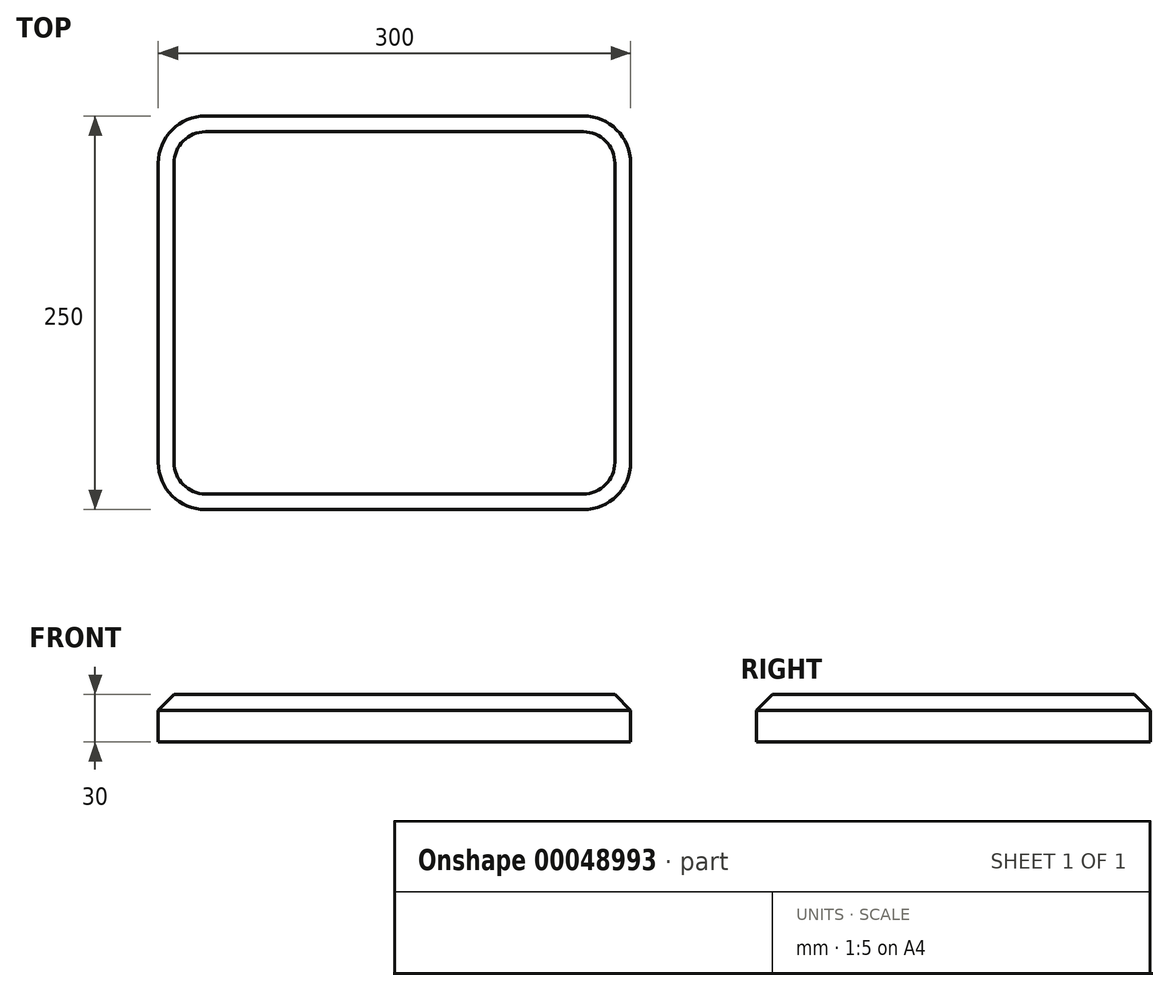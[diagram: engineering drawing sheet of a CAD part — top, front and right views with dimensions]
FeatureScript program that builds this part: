
annotation { "Feature Type Name" : "Feature", "Feature Type Description" : "" }
export const myFeature = defineFeature(function(context is Context, id is Id, definition is map)
    precondition{}
    {
        {
            var Q0;
            Q0=qCreatedBy(makeId("Top.planeOp"),FACE);
            var sketch = newSketch(context, id + "F0", { "sketchPlane" : qUnion([Q0])});
            skLineSegment(sketch, "E0.rect.bottom", {"start": v(150, 125) * mm, "end": v(-150, 125) * mm});
            skLineSegment(sketch, "E0.rect.top", {"start": v(150, -125) * mm, "end": v(-150, -125) * mm});
            skLineSegment(sketch, "E0.rect.left", {"start": v(150, 125) * mm, "end": v(150, -125) * mm});
            skLineSegment(sketch, "E0.rect.right", {"start": v(-150, 125) * mm, "end": v(-150, -125) * mm});
            skPoint(sketch, "E0.rect.middle", {"position": v(0, 0) * mm});
            skSolve(sketch);
        }
        {
            var Q0;
            Q0=makeQuery(id+"F0.imprint","IMPRINT",FACE,{"disambiguationData":[TD([[makeQuery(id+"F0.imprint","IMPRINT",EDGE,{"derivedFrom":sQuery(id+"F0.wireOp",EDGE,"E0.rect.bottom")}),1.0]])]});
            extrude(context, id + "F1", {"entities" : qUnion([Q0]), "depth" : 30 * mm});
        }
        {
            var Q0;
            Q0=makeQuery(id+"F3.opChamfer","BLEND_EDGE",EDGE,{"blendedFrom":[makeQuery(id+"F1.opExtrude","CAP_EDGE",EDGE,{"disambiguationData":[OSD([sQuery(id+"F0.wireOp",EDGE,"E0.rect.top")])],"isStart":false}),makeQuery(id+"F1.opExtrude","CAP_EDGE",EDGE,{"disambiguationData":[OSD([sQuery(id+"F0.wireOp",EDGE,"E0.rect.right")])],"isStart":false})],"blendedInto":[]});
            var Q1;
            Q1=makeQuery(id+"F3.opChamfer","BLEND_EDGE",EDGE,{"blendedFrom":[makeQuery(id+"F1.opExtrude","CAP_EDGE",EDGE,{"disambiguationData":[OSD([sQuery(id+"F0.wireOp",EDGE,"E0.rect.bottom")])],"isStart":false}),makeQuery(id+"F1.opExtrude","CAP_EDGE",EDGE,{"disambiguationData":[OSD([sQuery(id+"F0.wireOp",EDGE,"E0.rect.right")])],"isStart":false})],"blendedInto":[]});
            var Q2;
            Q2=makeQuery(id+"F3.opChamfer","BLEND_EDGE",EDGE,{"blendedFrom":[makeQuery(id+"F1.opExtrude","CAP_EDGE",EDGE,{"disambiguationData":[OSD([sQuery(id+"F0.wireOp",EDGE,"E0.rect.top")])],"isStart":false}),makeQuery(id+"F1.opExtrude","CAP_EDGE",EDGE,{"disambiguationData":[OSD([sQuery(id+"F0.wireOp",EDGE,"E0.rect.left")])],"isStart":false})],"blendedInto":[]});
            var Q3;
            Q3=makeQuery(id+"F3.opChamfer","BLEND_EDGE",EDGE,{"blendedFrom":[makeQuery(id+"F1.opExtrude","CAP_EDGE",EDGE,{"disambiguationData":[OSD([sQuery(id+"F0.wireOp",EDGE,"E0.rect.bottom")])],"isStart":false}),makeQuery(id+"F1.opExtrude","CAP_EDGE",EDGE,{"disambiguationData":[OSD([sQuery(id+"F0.wireOp",EDGE,"E0.rect.left")])],"isStart":false})],"blendedInto":[]});
            var Q4;
            Q4=makeQuery(id+"F1.opExtrude","SWEPT_EDGE",EDGE,{"disambiguationData":[OSD([sQuery(id+"F0.wireOp",EDGE,"E0.rect.top"),sQuery(id+"F0.wireOp",EDGE,"E0.rect.right")])]});
            var Q5;
            Q5=makeQuery(id+"F1.opExtrude","SWEPT_EDGE",EDGE,{"disambiguationData":[OSD([sQuery(id+"F0.wireOp",EDGE,"E0.rect.bottom"),sQuery(id+"F0.wireOp",EDGE,"E0.rect.right")])]});
            var Q6;
            Q6=makeQuery(id+"F1.opExtrude","SWEPT_EDGE",EDGE,{"disambiguationData":[OSD([sQuery(id+"F0.wireOp",EDGE,"E0.rect.bottom"),sQuery(id+"F0.wireOp",EDGE,"E0.rect.left")])]});
            var Q7;
            Q7=makeQuery(id+"F1.opExtrude","SWEPT_EDGE",EDGE,{"disambiguationData":[OSD([sQuery(id+"F0.wireOp",EDGE,"E0.rect.top"),sQuery(id+"F0.wireOp",EDGE,"E0.rect.left")])]});
            fillet(context, id + "F2", {"entities" : qUnion([Q0, Q1, Q2, Q3, Q4, Q5, Q6, Q7]), "radius" : 30 * mm, "tangentPropagation" : true, "allowEdgeOverflow" : false});
        }
        {
            var Q0;
            Q0=makeQuery(id+"F1.opExtrude","CAP_EDGE",EDGE,{"disambiguationData":[OSD([sQuery(id+"F0.wireOp",EDGE,"E0.rect.right")])],"isStart":false});
            var Q1;
            Q1=makeQuery(id+"F1.opExtrude","CAP_EDGE",EDGE,{"disambiguationData":[OSD([sQuery(id+"F0.wireOp",EDGE,"E0.rect.bottom")])],"isStart":false});
            var Q2;
            Q2=makeQuery(id+"F1.opExtrude","CAP_EDGE",EDGE,{"disambiguationData":[OSD([sQuery(id+"F0.wireOp",EDGE,"E0.rect.left")])],"isStart":false});
            var Q3;
            Q3=makeQuery(id+"F1.opExtrude","CAP_EDGE",EDGE,{"disambiguationData":[OSD([sQuery(id+"F0.wireOp",EDGE,"E0.rect.top")])],"isStart":false});
            chamfer(context, id + "F3", {"entities" : qUnion([Q0, Q1, Q2, Q3]), "chamferType" : ChamferType.OFFSET_ANGLE, "width" : 10 * mm, "oppositeDirection" : false, "angle" : 45 * degree, "tangentPropagation" : true});
        }
    });
